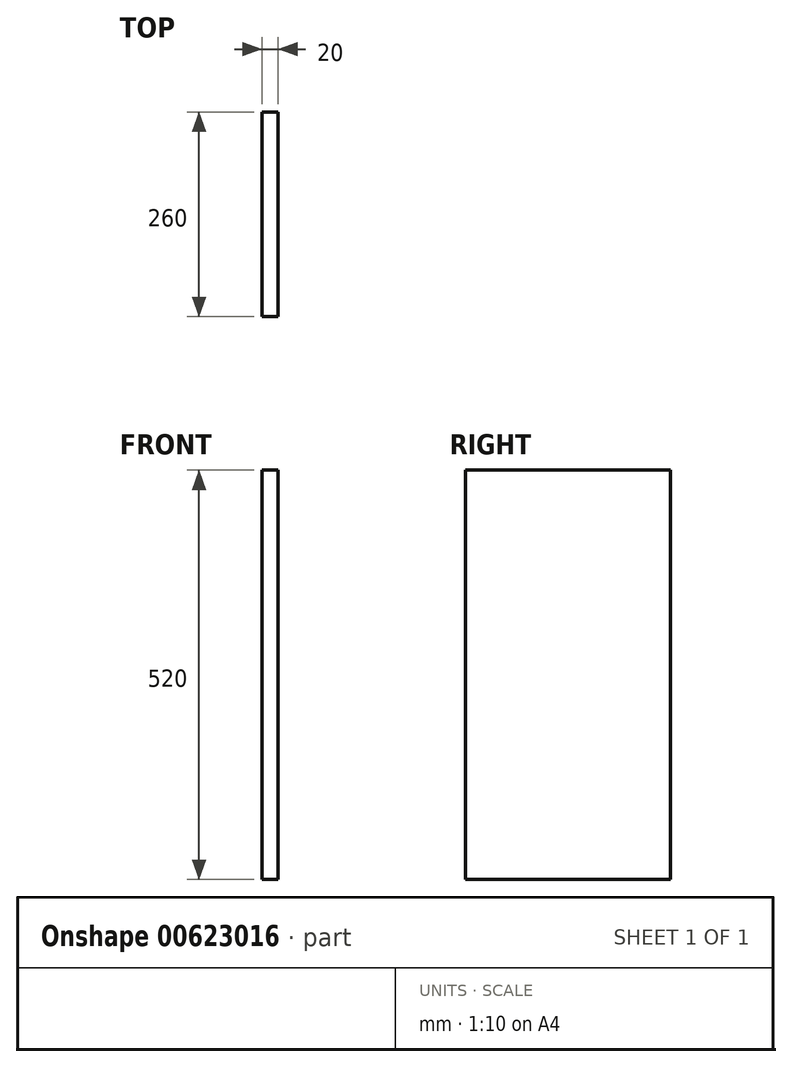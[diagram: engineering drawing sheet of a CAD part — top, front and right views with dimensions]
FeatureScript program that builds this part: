
annotation { "Feature Type Name" : "Feature", "Feature Type Description" : "" }
export const myFeature = defineFeature(function(context is Context, id is Id, definition is map)
    precondition{}
    {
        {
            var Q0;
            Q0=qCreatedBy(makeId("Right.planeOp"),FACE);
            var sketch = newSketch(context, id + "F0", { "sketchPlane" : qUnion([Q0])});
            skLineSegment(sketch, "E0.bottom", {"start": v(-260, -55.35) * mm, "end": v(0, -55.35) * mm});
            skLineSegment(sketch, "E0.top", {"start": v(-260, 464.65) * mm, "end": v(0, 464.65) * mm});
            skLineSegment(sketch, "E0.left", {"start": v(-260, -55.35) * mm, "end": v(-260, 464.65) * mm});
            skLineSegment(sketch, "E0.right", {"start": v(0, -55.35) * mm, "end": v(0, 464.65) * mm});
            skSolve(sketch);
        }
        {
            var Q0;
            Q0 = qSketchRegion(id + "F0", true);
            extrude(context, id + "F1", {"entities" : qUnion([Q0]), "depth" : 20 * mm, "offsetDistance" : 25 * mm});
        }
    });
